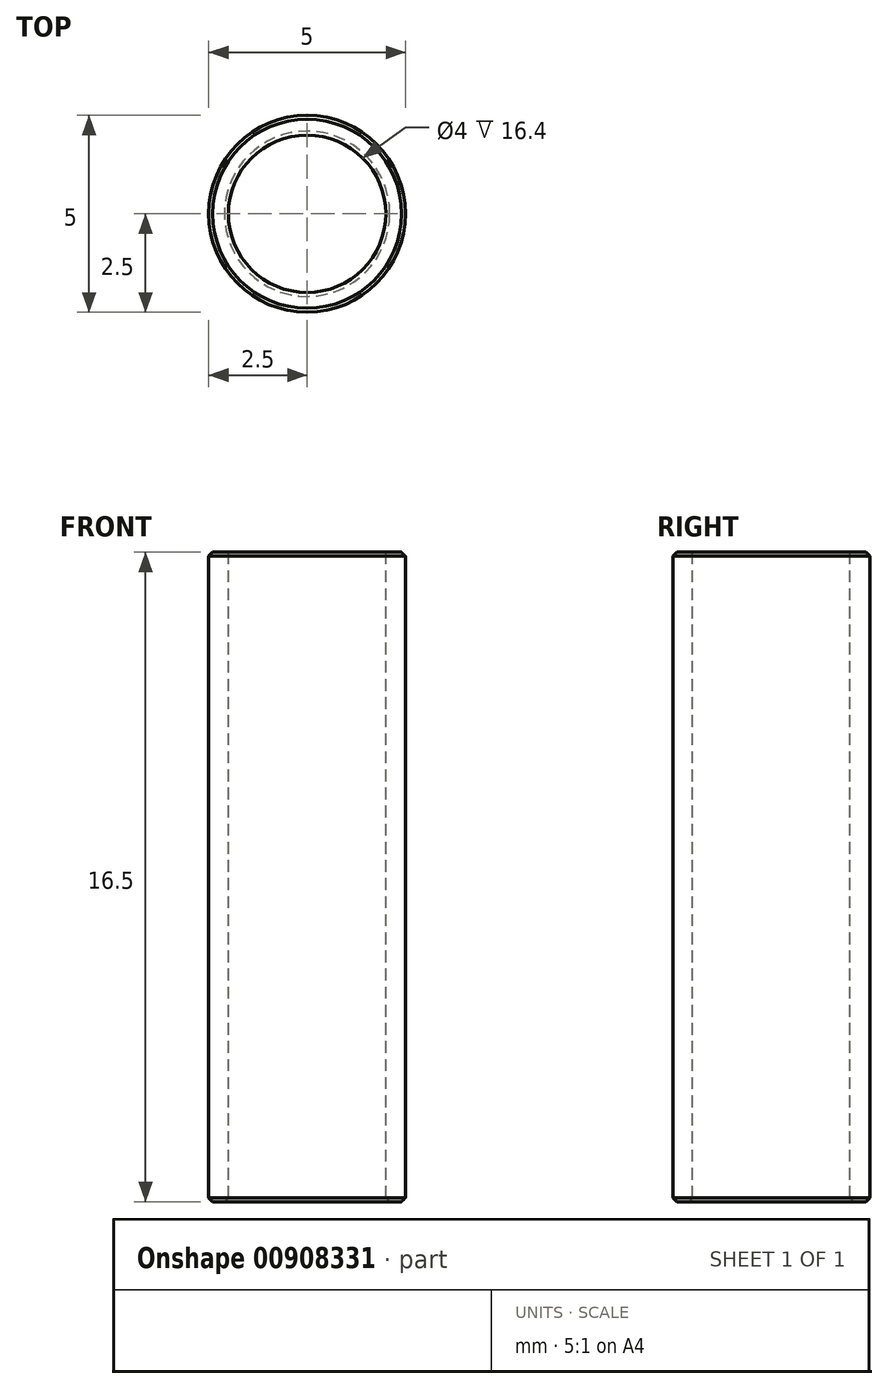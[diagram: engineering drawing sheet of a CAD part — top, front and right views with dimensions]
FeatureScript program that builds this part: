
annotation { "Feature Type Name" : "Feature", "Feature Type Description" : "" }
export const myFeature = defineFeature(function(context is Context, id is Id, definition is map)
    precondition{}
    {
        {
            var Q0;
            Q0=qCreatedBy(makeId("Top.planeOp"),FACE);
            var sketch = newSketch(context, id + "F0", { "sketchPlane" : qUnion([Q0])});
            skCircle(sketch, "E0", {"center": v(0, 0) * mm, "radius": 2.5 * mm});
            skSolve(sketch);
        }
        {
            var Q0;
            Q0 = qSketchRegion(id + "F0", true);
            extrude(context, id + "F1", {"entities" : qUnion([Q0]), "depth" : 16.5 * mm, "offsetDistance" : 25 * mm});
        }
        {
            var Q0;
            Q0=makeQuery(id+"F1.opExtrude","CAP_FACE",FACE,{"disambiguationData":[OSD([sQuery(id+"F0.wireOp",EDGE,"E0")])],"isStart":false});
            var sketch = newSketch(context, id + "F2", { "sketchPlane" : qUnion([Q0])});
            skCircle(sketch, "E1", {"center": v(0, 0) * mm, "radius": 2 * mm});
            skSolve(sketch);
        }
        {
            var Q0;
            Q0 = qSketchRegion(id + "F2", true);
            extrude(context, id + "F3", {"entities" : qUnion([Q0]), "operationType" : NewBodyOperationType.REMOVE, "endBound" : BoundingType.THROUGH_ALL, "oppositeDirection" : true, "depth" : 11 * mm, "offsetDistance" : 25 * mm});
        }
        {
            var Q0;
            Q0=makeQuery(id+"F3.boolean.opBoolean","INTERSECT",EDGE,{"derivedFrom":[makeQuery(id+"F1.opExtrude","CAP_FACE",FACE,{"disambiguationData":[OSD([sQuery(id+"F0.wireOp",EDGE,"E0")])],"isStart":true}),makeQuery(id+"F3.opExtrude","SWEPT_FACE",FACE,{"disambiguationData":[OSD([sQuery(id+"F2.wireOp",EDGE,"E1")])]})]});
            var Q1;
            Q1=makeQuery(id+"F1.opExtrude","CAP_EDGE",EDGE,{"disambiguationData":[OSD([sQuery(id+"F0.wireOp",EDGE,"E0")])],"isStart":true});
            var Q2;
            Q2=makeQuery(id+"F1.opExtrude","CAP_EDGE",EDGE,{"disambiguationData":[OSD([sQuery(id+"F0.wireOp",EDGE,"E0")])],"isStart":false});
            var Q3;
            Q3=makeQuery(id+"F3.boolean.opBoolean","COPY",EDGE,{"derivedFrom":makeQuery(id+"F3.opExtrude","CAP_EDGE",EDGE,{"disambiguationData":[OSD([sQuery(id+"F2.wireOp",EDGE,"E1")])],"isStart":true})});
            chamfer(context, id + "F4", {"entities" : qUnion([Q0, Q1, Q2, Q3]), "width" : .1 * mm, "tangentPropagation" : true});
        }
    });
